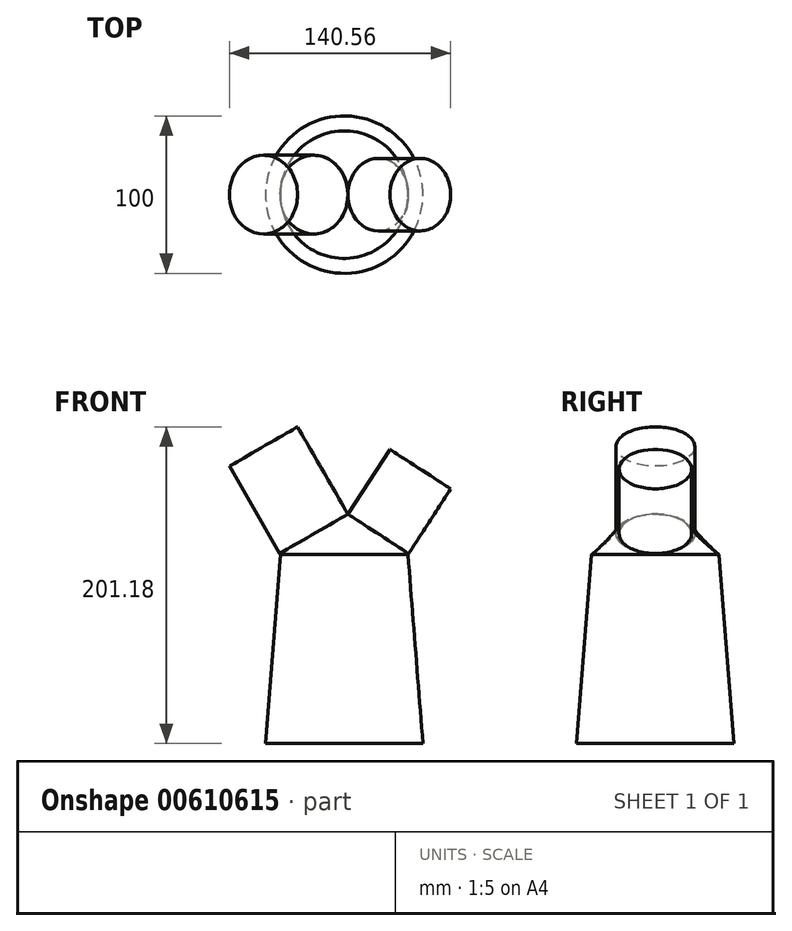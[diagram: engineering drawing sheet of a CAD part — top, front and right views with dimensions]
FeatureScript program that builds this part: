
annotation { "Feature Type Name" : "Feature", "Feature Type Description" : "" }
export const myFeature = defineFeature(function(context is Context, id is Id, definition is map)
    precondition{}
    {
        {
            assignVariable(context, id + "F0", {"name" : "H", "anyValue" : 120});
        }
        {
            var Q0;
            Q0=qCreatedBy(makeId("Top.planeOp"),FACE);
            var sketch = newSketch(context, id + "F1", { "sketchPlane" : qUnion([Q0])});
            skCircle(sketch, "E0", {"center": v(0, 0) * mm, "radius": 50 * mm});
            skSolve(sketch);
        }
        {
            var Q0;
            Q0=qCreatedBy(makeId("Top.planeOp"),FACE);
            cPlane(context, id + "F2", {"entities" : qUnion([Q0]), "cplaneType" : CPlaneType.OFFSET, "offset" : getVariable(context, 'H') * mm, "width" : 150 * mm, "height" : 150 * mm});
        }
        {
            var Q0;
            Q0=qCreatedBy(id+"F2.planeOp",FACE);
            var sketch = newSketch(context, id + "F3", { "sketchPlane" : qUnion([Q0])});
            skCircle(sketch, "E1", {"center": v(0, 0) * mm, "radius": 40.5 * mm});
            skLineSegment(sketch, "E2", {"start": v(-40.5, 0) * mm, "end": v(-40.5, 41.79) * mm, "construction": true});
            skLineSegment(sketch, "E3", {"start": v(40.5, 0) * mm, "end": v(40.5, 41.79) * mm, "construction": true});
            skSolve(sketch);
        }
        {
            var Q0;
            Q0=makeQuery(id+"F1.imprint","IMPRINT",FACE,{"disambiguationData":[TD([[makeQuery(id+"F1.imprint","IMPRINT",EDGE,{"derivedFrom":sQuery(id+"F1.wireOp",EDGE,"E0")}),1.0]])]});
            var Q1;
            Q1=makeQuery(id+"F3.imprint","IMPRINT",FACE,{"disambiguationData":[TD([[makeQuery(id+"F3.imprint","IMPRINT",EDGE,{"derivedFrom":sQuery(id+"F3.wireOp",EDGE,"E1")}),1.0]])]});
            loft(context, id + "F4", {"sheetProfilesArray" : [{ "sheetProfileEntities" : qUnion([Q0]) }, { "sheetProfileEntities" : qUnion([Q1]) }]});
        }
        {
            var Q0;
            Q0=qCreatedBy(makeId("Front.planeOp"),FACE);
            var sketch = newSketch(context, id + "F5", { "sketchPlane" : qUnion([Q0])});
            skLineSegment(sketch, "E4.0", {"start": v(-40.5, 120) * mm, "end": v(40.5, 120) * mm, "construction": true});
            skPoint(sketch, "E5", {"position": v(-40.5, 121) * mm});
            skPoint(sketch, "E6", {"position": v(40.5, 121) * mm});
            skSolve(sketch);
        }
        {
            var Q0;
            Q0=makeQuery(id+"F3.imprint","IMPRINT",FACE,{"disambiguationData":[TD([[makeQuery(id+"F3.imprint","IMPRINT",EDGE,{"derivedFrom":sQuery(id+"F3.wireOp",EDGE,"E1")}),1.0]])]});
            var Q1;
            Q1=sQuery(id+"F5.wireOp",VERTEX,"E5");
            cPlane(context, id + "F6", {"entities" : qUnion([Q0, Q1]), "cplaneType" : CPlaneType.PLANE_POINT, "offset" : 25 * mm, "width" : 150 * mm, "height" : 150 * mm});
        }
        {
            var Q0;
            Q0=qCreatedBy(id+"F6.planeOp",FACE);
            var sketch = newSketch(context, id + "F7", { "sketchPlane" : qUnion([Q0])});
            skLineSegment(sketch, "E7.0", {"start": v(-40.5, 0) * mm, "end": v(-40.5, 41.79) * mm, "construction": true});
            skLineSegment(sketch, "E8.0", {"start": v(40.5, 0) * mm, "end": v(40.5, 41.79) * mm, "construction": true});
            skSolve(sketch);
        }
        {
            var Q0;
            Q0=sQuery(id+"F7.wireOp",EDGE,"E7.0");
            cPlane(context, id + "F8", {"entities" : qUnion([Q0]), "cplaneType" : CPlaneType.LINE_ANGLE, "offset" : 25 * mm, "angle" : 30 * degree, "oppositeDirection" : true, "width" : 150 * mm, "height" : 150 * mm});
        }
        {
            var Q0;
            Q0=qCreatedBy(id+"F8.planeOp",FACE);
            var sketch = newSketch(context, id + "F9", { "sketchPlane" : qUnion([Q0])});
            skLineSegment(sketch, "E9.0", {"start": v(24.93, 0) * mm, "end": v(24.93, 41.79) * mm, "construction": true});
            skCircle(sketch, "E10", {"center": v(49.93, 0) * mm, "radius": 25 * mm});
            skPoint(sketch, "E11", {"position": v(74.93, 0) * mm});
            skSolve(sketch);
        }
        {
            var Q0;
            Q0=sQuery(id+"F7.wireOp",EDGE,"E8.0");
            var Q1;
            Q1=sQuery(id+"F9.wireOp",VERTEX,"E11");
            cPlane(context, id + "F10", {"entities" : qUnion([Q0, Q1]), "cplaneType" : CPlaneType.LINE_ANGLE, "offset" : 25 * mm, "angle" : 0 * degree, "width" : 150 * mm, "height" : 150 * mm});
        }
        {
            var Q0;
            Q0=qCreatedBy(id+"F10.planeOp",FACE);
            var sketch = newSketch(context, id + "F11", { "sketchPlane" : qUnion([Q0])});
            skPoint(sketch, "E12.0", {"position": v(-77.37, 0) * mm});
            skLineSegment(sketch, "E13.0", {"start": v(-31.36, 0) * mm, "end": v(-31.36, 41.79) * mm, "construction": true});
            skCircle(sketch, "E14", {"center": v(-54.36, 0) * mm, "radius": 23 * mm});
            skSolve(sketch);
        }
        {
            var Q0;
            Q0=makeQuery(id+"F4.opLoft","CAP_FACE",FACE,{"disambiguationData":[OSD([makeQuery(id+"F3.imprint","IMPRINT",FACE,{"disambiguationData":[TD([[makeQuery(id+"F3.imprint","IMPRINT",EDGE,{"derivedFrom":sQuery(id+"F3.wireOp",EDGE,"E1")}),1.0]])]})])],"isStart":true});
            var Q1;
            Q1=makeQuery(id+"F9.imprint","IMPRINT",FACE,{"disambiguationData":[TD([[makeQuery(id+"F9.imprint","IMPRINT",EDGE,{"derivedFrom":sQuery(id+"F9.wireOp",EDGE,"E10")}),1.0]])]});
            loft(context, id + "F12", {"sheetProfilesArray" : [{ "sheetProfileEntities" : qUnion([Q0]) }, { "sheetProfileEntities" : qUnion([Q1]) }]});
        }
        {
            var Q0;
            Q0=makeQuery(id+"F4.opLoft","CAP_FACE",FACE,{"disambiguationData":[OSD([makeQuery(id+"F3.imprint","IMPRINT",FACE,{"disambiguationData":[TD([[makeQuery(id+"F3.imprint","IMPRINT",EDGE,{"derivedFrom":sQuery(id+"F3.wireOp",EDGE,"E1")}),1.0]])]})])],"isStart":true});
            var Q1;
            Q1=makeQuery(id+"F11.imprint","IMPRINT",FACE,{"disambiguationData":[TD([[makeQuery(id+"F11.imprint","IMPRINT",EDGE,{"derivedFrom":sQuery(id+"F11.wireOp",EDGE,"E14")}),1.0]])]});
            loft(context, id + "F13", {"sheetProfilesArray" : [{ "sheetProfileEntities" : qUnion([Q0]) }, { "sheetProfileEntities" : qUnion([Q1]) }]});
        }
        {
            var Q0;
            Q0=makeQuery(id+"F9.imprint","IMPRINT",FACE,{"disambiguationData":[TD([[makeQuery(id+"F9.imprint","IMPRINT",EDGE,{"derivedFrom":sQuery(id+"F9.wireOp",EDGE,"E10")}),1.0]])]});
            extrude(context, id + "F14", {"entities" : qUnion([Q0]), "depth" : 64 * mm, "offsetDistance" : 25 * mm});
        }
        {
            var Q0;
            Q0=makeQuery(id+"F13.opLoft","CAP_FACE",FACE,{"disambiguationData":[OSD([makeQuery(id+"F11.imprint","IMPRINT",FACE,{"disambiguationData":[TD([[makeQuery(id+"F11.imprint","IMPRINT",EDGE,{"derivedFrom":sQuery(id+"F11.wireOp",EDGE,"E14")}),1.0]])]})])],"isStart":true});
            extrude(context, id + "F15", {"entities" : qUnion([Q0]), "depth" : 49 * mm, "offsetDistance" : 25 * mm});
        }
    });
